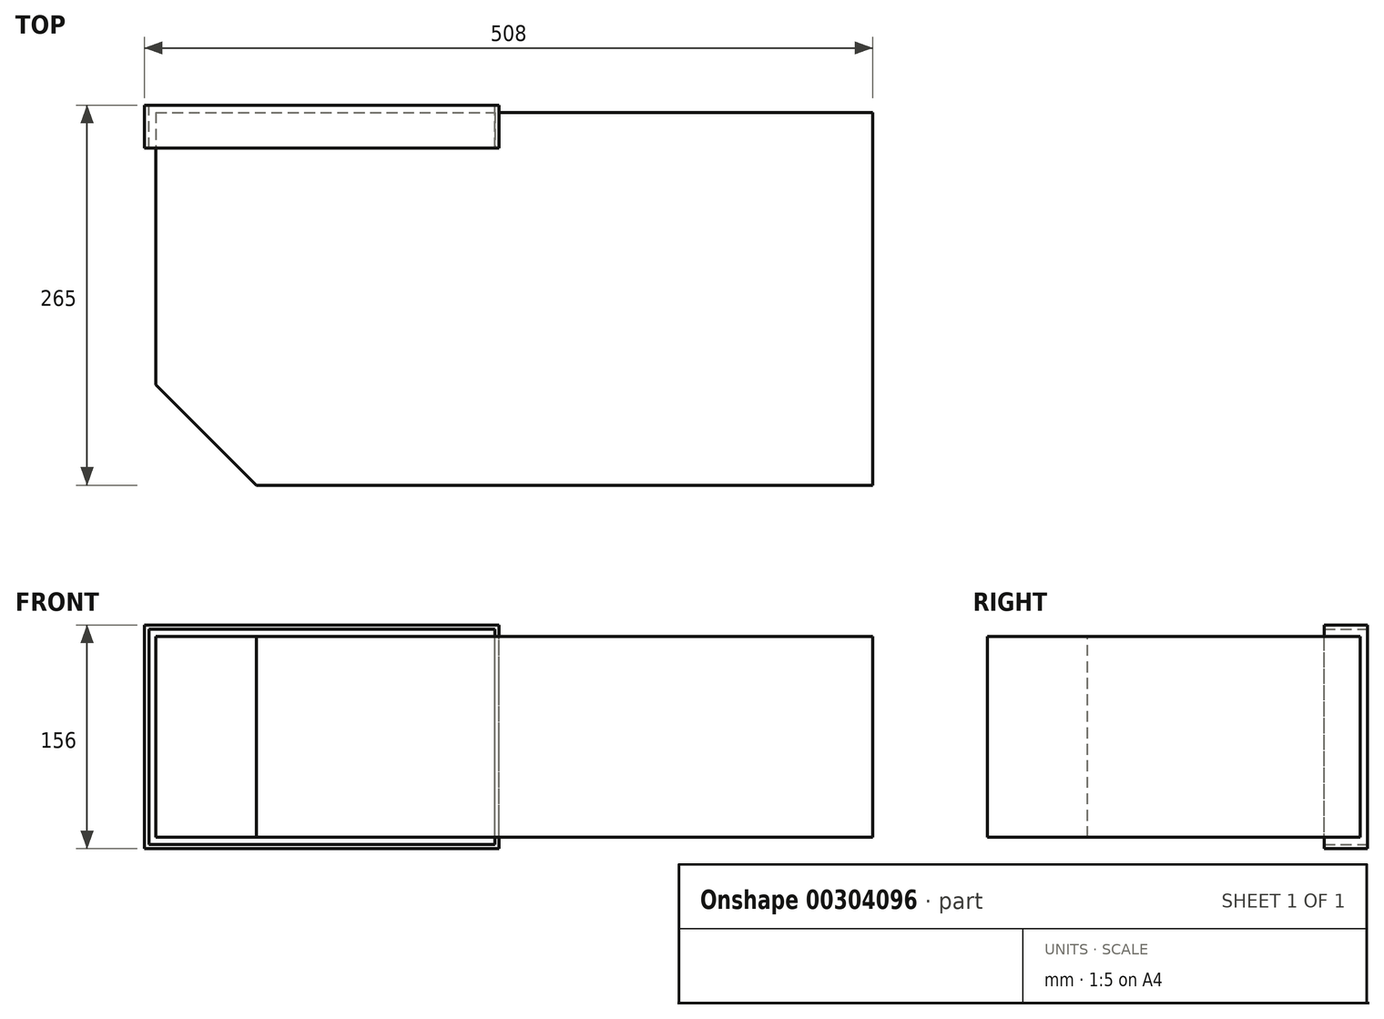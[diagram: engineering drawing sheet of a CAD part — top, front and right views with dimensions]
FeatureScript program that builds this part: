
annotation { "Feature Type Name" : "Feature", "Feature Type Description" : "" }
export const myFeature = defineFeature(function(context is Context, id is Id, definition is map)
    precondition{}
    {
        {
            var Q0;
            Q0=qCreatedBy(makeId("Top.planeOp"),FACE);
            var sketch = newSketch(context, id + "F0", { "sketchPlane" : qUnion([Q0])});
            skLineSegment(sketch, "E0.bottom", {"start": v(-196.24, 124.95) * mm, "end": v(303.76, 124.95) * mm});
            skLineSegment(sketch, "E0.top", {"start": v(-196.24, -135.05) * mm, "end": v(303.76, -135.05) * mm});
            skLineSegment(sketch, "E0.left", {"start": v(-196.24, 124.95) * mm, "end": v(-196.24, -135.05) * mm});
            skLineSegment(sketch, "E0.right", {"start": v(303.76, 124.95) * mm, "end": v(303.76, -135.05) * mm});
            skSolve(sketch);
        }
        {
            var Q0;
            Q0=makeQuery(id+"F0.imprint","IMPRINT",FACE,{"disambiguationData":[TD([[makeQuery(id+"F0.imprint","IMPRINT",EDGE,{"derivedFrom":sQuery(id+"F0.wireOp",EDGE,"E0.bottom")}),-1.0]])]});
            extrude(context, id + "F1", {"entities" : qUnion([Q0]), "depth" : 140 * mm, "offsetDistance" : 25 * mm});
        }
        {
            var Q0;
            Q0=makeQuery(id+"F1.opExtrude","SWEPT_EDGE",EDGE,{"disambiguationData":[OSD([sQuery(id+"F0.wireOp",EDGE,"E0.top"),sQuery(id+"F0.wireOp",EDGE,"E0.left")])]});
            chamfer(context, id + "F2", {"entities" : qUnion([Q0]), "width" : 70 * mm, "tangentPropagation" : true});
        }
        {
            var Q0;
            Q0=makeQuery(id+"F1.opExtrude","SWEPT_FACE",FACE,{"disambiguationData":[OSD([sQuery(id+"F0.wireOp",EDGE,"E0.bottom")])]});
            cPlane(context, id + "F3", {"entities" : qUnion([Q0]), "cplaneType" : CPlaneType.OFFSET, "offset" : 5 * mm, "width" : 150 * mm, "height" : 150 * mm});
        }
        {
            var Q0;
            Q0=qCreatedBy(id+"F3.planeOp",FACE);
            var sketch = newSketch(context, id + "F4", { "sketchPlane" : qUnion([Q0])});
            skLineSegment(sketch, "E1.bottom", {"start": v(-40.05, -5) * mm, "end": v(201.24, -5) * mm});
            skLineSegment(sketch, "E1.top", {"start": v(-40.05, 145) * mm, "end": v(201.24, 145) * mm});
            skLineSegment(sketch, "E1.left", {"start": v(-40.05, -5) * mm, "end": v(-40.05, 145) * mm});
            skLineSegment(sketch, "E1.right", {"start": v(201.24, -5) * mm, "end": v(201.24, 145) * mm});
            skLineSegment(sketch, "E2.0", {"start": v(-43.05, -8) * mm, "end": v(204.24, -8) * mm});
            skLineSegment(sketch, "E2.1", {"start": v(-43.05, -8) * mm, "end": v(-43.05, 148) * mm});
            skLineSegment(sketch, "E2.2", {"start": v(-43.05, 148) * mm, "end": v(204.24, 148) * mm});
            skLineSegment(sketch, "E2.3", {"start": v(204.24, -8) * mm, "end": v(204.24, 148) * mm});
            skSolve(sketch);
        }
        {
            var Q0;
            Q0=makeQuery(id+"F4.imprint","IMPRINT",FACE,{"disambiguationData":[TD([[makeQuery(id+"F4.imprint","IMPRINT",EDGE,{"derivedFrom":sQuery(id+"F4.wireOp",EDGE,"E1.bottom")}),-1.0]])]});
            extrude(context, id + "F5", {"entities" : qUnion([Q0]), "operationType" : NewBodyOperationType.ADD, "oppositeDirection" : true, "depth" : 30 * mm, "offsetDistance" : 25 * mm});
        }
    });
